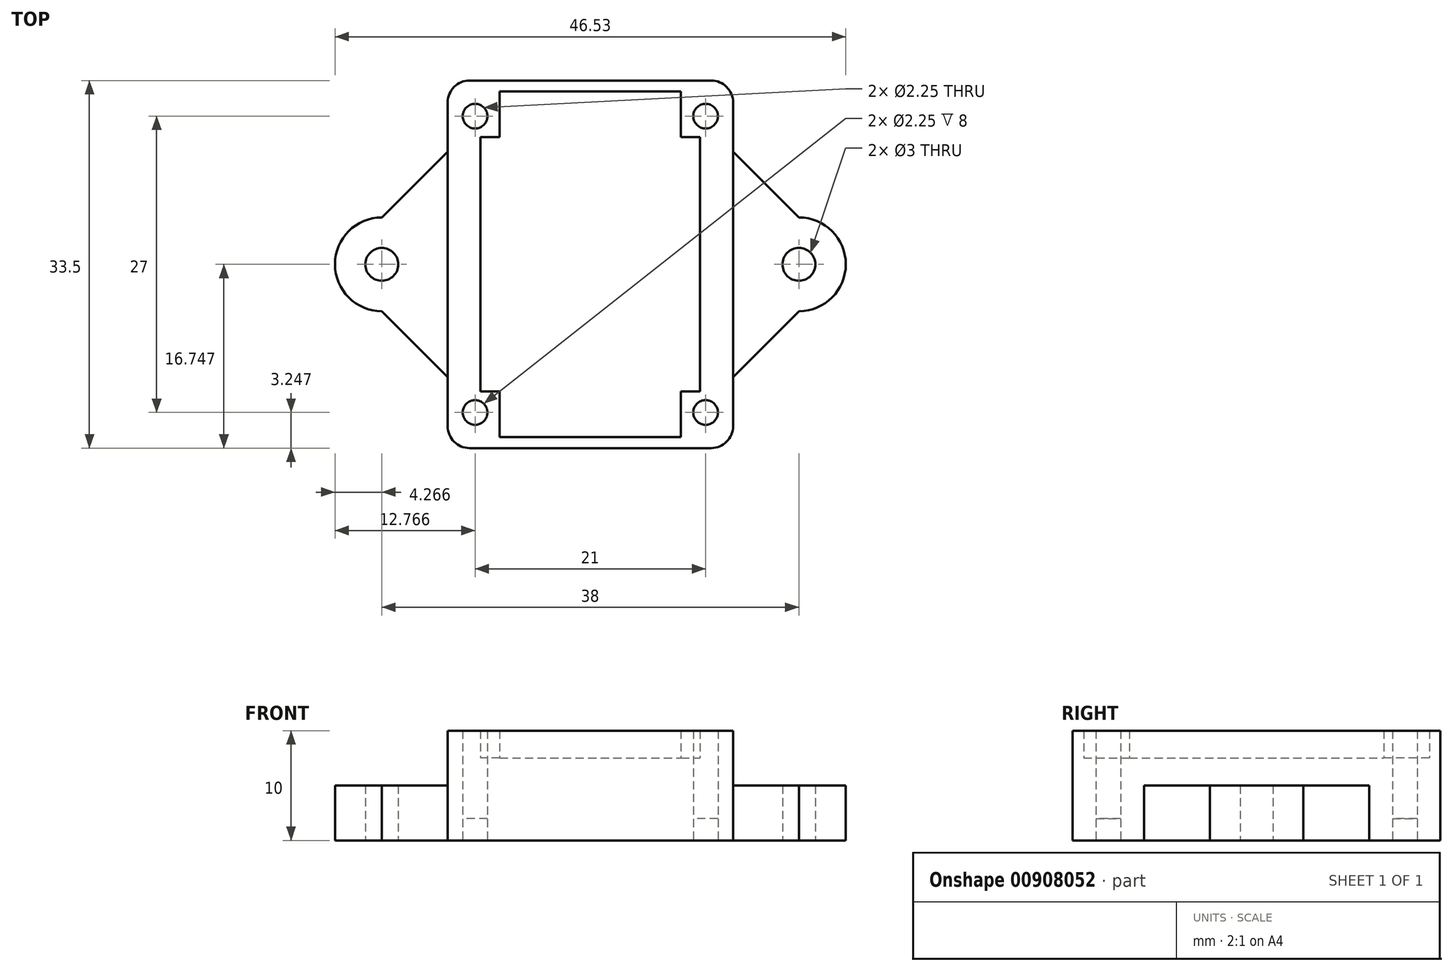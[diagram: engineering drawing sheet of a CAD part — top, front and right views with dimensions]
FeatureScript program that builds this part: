
annotation { "Feature Type Name" : "Feature", "Feature Type Description" : "" }
export const myFeature = defineFeature(function(context is Context, id is Id, definition is map)
    precondition{}
    {
        {
            var Q0;
            Q0=qCreatedBy(makeId("Top.planeOp"),FACE);
            var Q1;
            Q1=qCreatedBy(makeId("Top.planeOp"),FACE);
            var Q2;
            Q2=qCreatedBy(makeId("Top.planeOp"),FACE);
            var Q3;
            Q3=qCreatedBy(makeId("Top.planeOp"),FACE);
            var Q4;
            Q4=qCreatedBy(makeId("Front.planeOp"),FACE);
            var Q5;
            Q5=qCreatedBy(makeId("Top.planeOp"),FACE);
            var sketch = newSketch(context, id + "F0", { "sketchPlane" : qUnion([Q0, Q1, Q2, Q3, Q4, Q5])});
            skLineSegment(sketch, "E0.bottom", {"start": v(-47.83, 31.34) * mm, "end": v(-25.83, 31.34) * mm});
            skLineSegment(sketch, "E0.top", {"start": v(-47.83, -2.16) * mm, "end": v(-25.83, -2.16) * mm});
            skLineSegment(sketch, "E0.left", {"start": v(-49.83, 29.34) * mm, "end": v(-49.83, -0.16) * mm});
            skLineSegment(sketch, "E0.right", {"start": v(-23.83, 29.34) * mm, "end": v(-23.83, -0.16) * mm});
            skPoint(sketch, "E1.visualSharp", {"position": v(-49.83, 31.34) * mm});
            skArc(sketch, "E1.filletArc", {"start": v(-47.83, 31.34) * mm, "mid": v(-49.25, 30.75) * mm, "end": v(-49.83, 29.34) * mm});
            skPoint(sketch, "E2.visualSharp", {"position": v(-23.83, 31.34) * mm});
            skArc(sketch, "E2.filletArc", {"start": v(-23.83, 29.34) * mm, "mid": v(-24.42, 30.75) * mm, "end": v(-25.83, 31.34) * mm});
            skPoint(sketch, "E3.visualSharp", {"position": v(-23.83, -2.16) * mm});
            skArc(sketch, "E3.filletArc", {"start": v(-25.83, -2.16) * mm, "mid": v(-24.42, -1.58) * mm, "end": v(-23.83, -0.16) * mm});
            skPoint(sketch, "E4.visualSharp", {"position": v(-49.83, -2.16) * mm});
            skArc(sketch, "E4.filletArc", {"start": v(-49.83, -0.16) * mm, "mid": v(-49.25, -1.58) * mm, "end": v(-47.83, -2.16) * mm});
            skCircle(sketch, "E5", {"center": v(-26.33, 28.09) * mm, "radius": 1.13 * mm});
            skLineSegment(sketch, "E6", {"start": v(-36.83, 31.34) * mm, "end": v(-36.83, -2.16) * mm, "construction": true});
            skLineSegment(sketch, "E7", {"start": v(-49.83, 14.59) * mm, "end": v(-23.83, 14.59) * mm, "construction": true});
            skCircle(sketch, "E8.MirrorC", {"center": v(-47.33, 28.09) * mm, "radius": 1.13 * mm});
            skLineSegment(sketch, "E9.MirrorCS", {"start": v(-23.83, 14.59) * mm, "end": v(-49.83, 14.59) * mm, "construction": true});
            skCircle(sketch, "E10.MirrorC", {"center": v(-47.33, 1.09) * mm, "radius": 1.13 * mm});
            skCircle(sketch, "E11.MirrorC", {"center": v(-26.33, 1.09) * mm, "radius": 1.13 * mm});
            skLineSegment(sketch, "E12", {"start": v(-36.83, 30.34) * mm, "end": v(-28.58, 30.34) * mm});
            skLineSegment(sketch, "E13", {"start": v(-28.58, 30.34) * mm, "end": v(-28.58, 26.18) * mm});
            skLineSegment(sketch, "E14", {"start": v(-28.58, 26.18) * mm, "end": v(-26.83, 26.18) * mm});
            skLineSegment(sketch, "E15", {"start": v(-26.83, 26.18) * mm, "end": v(-26.83, 14.59) * mm});
            skLineSegment(sketch, "E16.MirrorCS", {"start": v(-26.83, 2.99) * mm, "end": v(-26.83, 14.59) * mm});
            skLineSegment(sketch, "E17.MirrorCS", {"start": v(-28.58, 2.99) * mm, "end": v(-26.83, 2.99) * mm});
            skLineSegment(sketch, "E18.MirrorCS", {"start": v(-28.58, -1.16) * mm, "end": v(-28.58, 2.99) * mm});
            skLineSegment(sketch, "E19.MirrorCS", {"start": v(-36.83, -1.16) * mm, "end": v(-28.58, -1.16) * mm});
            skLineSegment(sketch, "E20.MirrorCS", {"start": v(-36.83, 30.34) * mm, "end": v(-45.1, 30.34) * mm});
            skLineSegment(sketch, "E21.MirrorCS", {"start": v(-45.1, 30.34) * mm, "end": v(-45.1, 26.18) * mm});
            skLineSegment(sketch, "E22.MirrorCS", {"start": v(-45.1, 26.18) * mm, "end": v(-46.83, 26.18) * mm});
            skLineSegment(sketch, "E23.MirrorCS", {"start": v(-46.83, 26.18) * mm, "end": v(-46.83, 14.59) * mm});
            skLineSegment(sketch, "E24.MirrorCS", {"start": v(-36.83, -1.16) * mm, "end": v(-45.1, -1.16) * mm});
            skLineSegment(sketch, "E25.MirrorCS", {"start": v(-45.1, -1.16) * mm, "end": v(-45.1, 2.99) * mm});
            skLineSegment(sketch, "E26.MirrorCS", {"start": v(-45.1, 2.99) * mm, "end": v(-46.83, 2.99) * mm});
            skLineSegment(sketch, "E27.MirrorCS", {"start": v(-46.83, 2.99) * mm, "end": v(-46.83, 14.59) * mm});
            skLineSegment(sketch, "E28", {"start": v(-49.83, 14.59) * mm, "end": v(-55.83, 14.59) * mm, "construction": true});
            skLineSegment(sketch, "E29", {"start": v(-55.83, 14.59) * mm, "end": v(-11.2, 14.59) * mm, "construction": true});
            skCircle(sketch, "E30", {"center": v(-55.83, 14.59) * mm, "radius": 1.5 * mm});
            skArc(sketch, "E31", {"start": v(-55.83, 18.85) * mm, "mid": v(-60.1, 14.59) * mm, "end": v(-55.83, 10.32) * mm});
            skLineSegment(sketch, "E32", {"start": v(-55.83, 14.59) * mm, "end": v(-60.1, 14.59) * mm, "construction": true});
            skLineSegment(sketch, "E33", {"start": v(-55.83, 10.32) * mm, "end": v(-49.83, 4.32) * mm});
            skLineSegment(sketch, "E34.MirrorCS", {"start": v(-55.83, 18.85) * mm, "end": v(-49.83, 24.85) * mm});
            skLineSegment(sketch, "E35.MirrorCS", {"start": v(-17.83, 18.85) * mm, "end": v(-23.83, 24.85) * mm});
            skArc(sketch, "E36.MirrorCS", {"start": v(-17.83, 18.85) * mm, "mid": v(-13.57, 14.59) * mm, "end": v(-17.83, 10.32) * mm});
            skCircle(sketch, "E37.MirrorC", {"center": v(-17.83, 14.59) * mm, "radius": 1.5 * mm});
            skLineSegment(sketch, "E38.MirrorCS", {"start": v(-17.83, 10.32) * mm, "end": v(-23.83, 4.32) * mm});
            skSolve(sketch);
        }
        {
            var Q0;
            Q0=makeQuery(id+"F0.imprint","IMPRINT",FACE,{"disambiguationData":[TD([[makeQuery(id+"F0.imprint","IMPRINT",EDGE,{"derivedFrom":sQuery(id+"F0.wireOp",EDGE,"E0.bottom")}),-1.0]])]});
            extrude(context, id + "F1", {"entities" : qUnion([Q0]), "depth" : 10 * mm, "offsetDistance" : 25 * mm});
        }
        {
            var Q0;
            Q0=makeQuery(id+"F0.imprint","IMPRINT",FACE,{"disambiguationData":[TD([[makeQuery(id+"F0.imprint","IMPRINT",EDGE,{"derivedFrom":sQuery(id+"F0.wireOp",EDGE,"E30")}),-1.0]])]});
            var Q1;
            {var subQ0=sQuery(id+"F0.wireOp",EDGE,"E35.MirrorCS");Q1=makeQuery(id+"F0.imprint","IMPRINT",FACE,{"disambiguationData":[TD([[makeQuery(id+"F0.imprint","IMPRINT",EDGE,{"derivedFrom":subQ0}),1.0]])]});}
            extrude(context, id + "F2", {"entities" : qUnion([Q0, Q1]), "operationType" : NewBodyOperationType.ADD, "depth" : 5 * mm, "offsetDistance" : 25 * mm});
        }
        {
            var Q0;
            Q0=makeQuery(id+"F0.imprint","IMPRINT",FACE,{"disambiguationData":[TD([[makeQuery(id+"F0.imprint","IMPRINT",EDGE,{"derivedFrom":sQuery(id+"F0.wireOp",EDGE,"E12")}),-1.0]])]});
            extrude(context, id + "F3", {"entities" : qUnion([Q0]), "operationType" : NewBodyOperationType.ADD, "depth" : 7.5 * mm, "offsetDistance" : 25 * mm});
        }
        {
            var Q0;
            Q0=makeQuery(id+"F0.imprint","IMPRINT",FACE,{"disambiguationData":[TD([[makeQuery(id+"F0.imprint","IMPRINT",EDGE,{"derivedFrom":sQuery(id+"F0.wireOp",EDGE,"E5")}),1.0]])]});
            var Q1;
            Q1=makeQuery(id+"F0.imprint","IMPRINT",FACE,{"disambiguationData":[TD([[makeQuery(id+"F0.imprint","IMPRINT",EDGE,{"derivedFrom":sQuery(id+"F0.wireOp",EDGE,"E8.MirrorC")}),-1.0]])]});
            var Q2;
            Q2=makeQuery(id+"F0.imprint","IMPRINT",FACE,{"disambiguationData":[TD([[makeQuery(id+"F0.imprint","IMPRINT",EDGE,{"derivedFrom":sQuery(id+"F0.wireOp",EDGE,"E11.MirrorC")}),-1.0]])]});
            var Q3;
            Q3=makeQuery(id+"F0.imprint","IMPRINT",FACE,{"disambiguationData":[TD([[makeQuery(id+"F0.imprint","IMPRINT",EDGE,{"derivedFrom":sQuery(id+"F0.wireOp",EDGE,"E10.MirrorC")}),1.0]])]});
            extrude(context, id + "F4", {"entities" : qUnion([Q0, Q1, Q2, Q3]), "operationType" : NewBodyOperationType.ADD, "depth" : 2 * mm, "offsetDistance" : 25 * mm});
        }
    });
